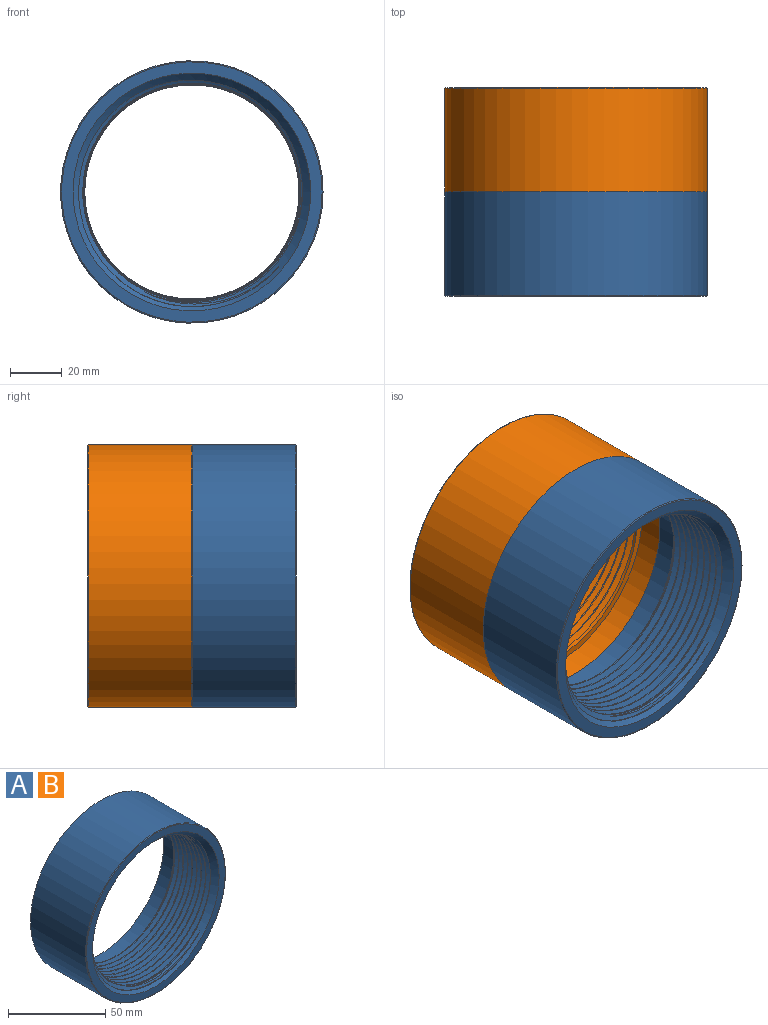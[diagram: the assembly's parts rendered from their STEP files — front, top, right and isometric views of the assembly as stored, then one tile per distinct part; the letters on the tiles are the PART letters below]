
ASSEMBLY  parts=2 mates=1
PART A: 13 faces, bbox 111.2x41.7x111.2 mm
  f0: plane 100.84x100.84mm, normal (0,-1,0), area 1327.7mm2, adj f4,f12
  f1: cylinder r=50.8mm len=101.6mm, axis (0,1,0), area 12769mm2, adj f2,f12
  f2: plane 101.6x101.6mm, normal (0,1,0), area 1448.9mm2, adj f1,f10
  f3: plane 61.38x46.85mm, normal (0,-1,0), area 35.6mm2, adj f4,f7,f8,f9
  f4: cone r=46.04mm half-angle=45deg, axis (0,-1,0), area 1020.1mm2, adj f0,f3,f6,f7,f9
  f5: plane 2.11x1.41mm, normal (1,0,0), area 1.7mm2, adj f6,f8,f9,f11
  f6: cone r=44.45mm half-angle=1.8deg, axis (0,-1,0), area 1565.8mm2, adj f4,f5,f7,f9,f11
  f7: bspline ~90.14x90.1mm, area 5524.3mm2, adj f3,f4,f6,f8,f11
  f8: bspline ~85.74x85.67mm, area 896.1mm2, adj f3,f5,f7,f9,f11
  f9: bspline ~90.45x90.37mm, area 5599.5mm2, adj f3,f4,f5,f6,f8
  f10: cylinder r=46.04mm len=92.08mm, axis (0,-1,0), area 2865.4mm2, adj f2,f11
  f11: plane 93.35x93.35mm, normal (0,1,0), area 849.9mm2, adj f5,f6,f7,f8,f10
  f12: torus R=50.42mm, axis (0,-1,0), area 190.5mm2, adj f0,f1
PART B: same geometry as A
PLACE A t=(0,19.81,0)mm
PLACE B rot(axis=(1,0,0),180deg) t=(0,60.2,0)mm
MATE fastened B.f1 <-> A.f1  axis (0,-1,0) through (0,40,0)mm
